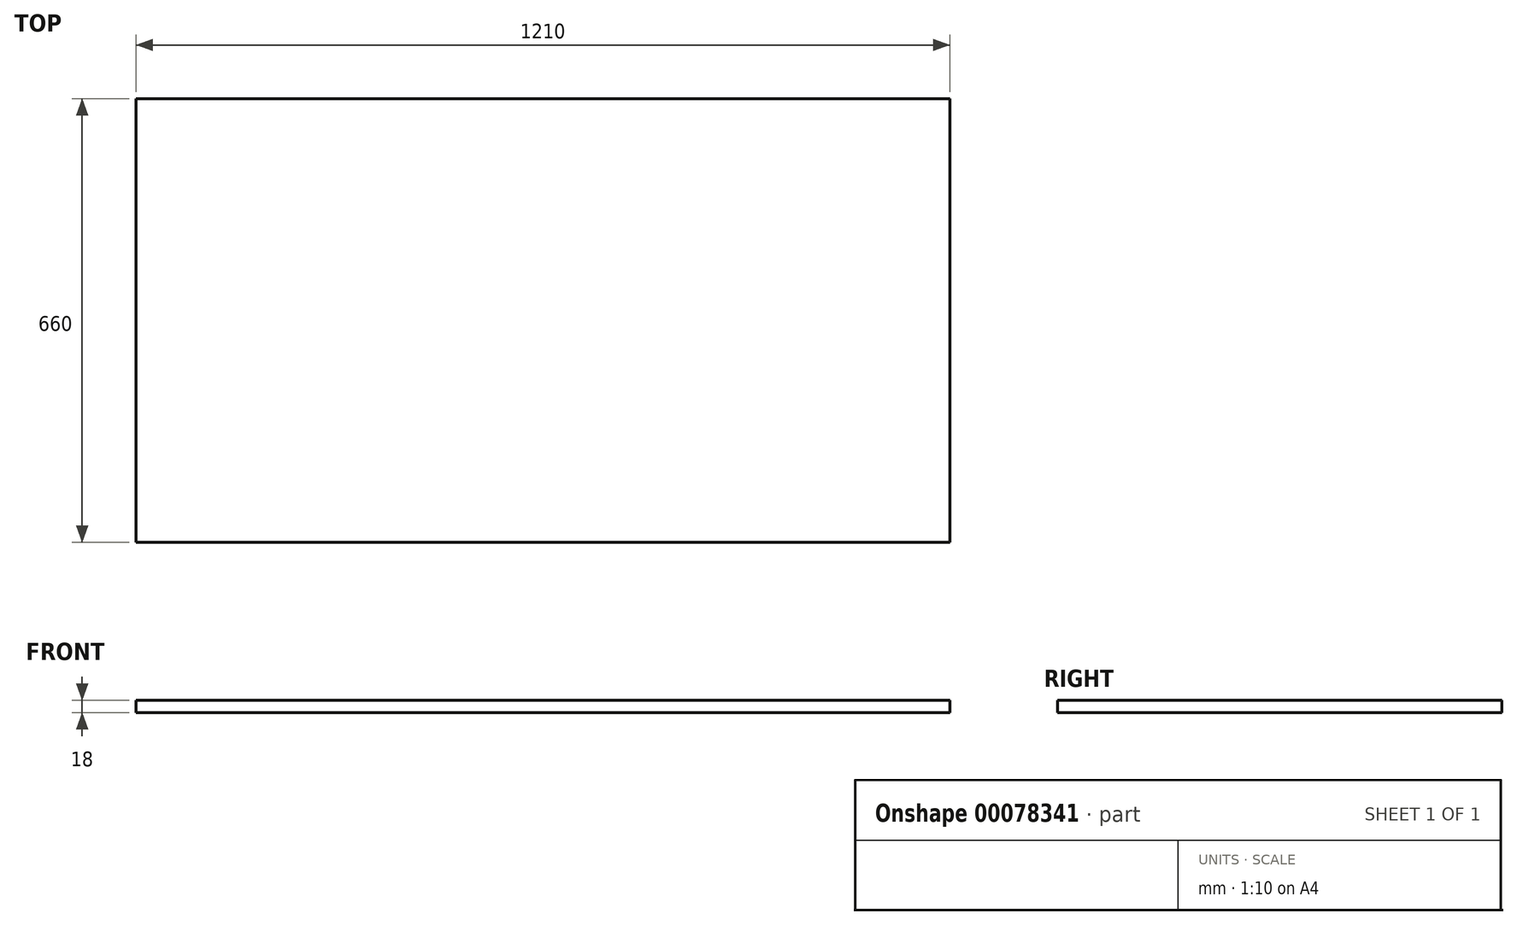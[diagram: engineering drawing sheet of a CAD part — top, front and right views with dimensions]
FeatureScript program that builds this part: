
annotation { "Feature Type Name" : "Feature", "Feature Type Description" : "" }
export const myFeature = defineFeature(function(context is Context, id is Id, definition is map)
    precondition{}
    {
        {
            var Q0;
            Q0=qCreatedBy(makeId("Top.planeOp"),FACE);
            var sketch = newSketch(context, id + "F0", { "sketchPlane" : qUnion([Q0])});
            skLineSegment(sketch, "E0", {"start": v(0, 0) * mm, "end": v(0, 935.46) * mm, "construction": true});
            skLineSegment(sketch, "E1.bottom", {"start": v(-605, 0) * mm, "end": v(605, 0) * mm});
            skLineSegment(sketch, "E1.top", {"start": v(-605, 660) * mm, "end": v(605, 660) * mm});
            skLineSegment(sketch, "E1.left", {"start": v(-605, 0) * mm, "end": v(-605, 660) * mm});
            skLineSegment(sketch, "E1.right", {"start": v(605, 0) * mm, "end": v(605, 660) * mm});
            skLineSegment(sketch, "E2.bottom", {"start": v(-402.5, 630) * mm, "end": v(-202.5, 630) * mm});
            skLineSegment(sketch, "E2.top", {"start": v(-402.5, 525) * mm, "end": v(-202.5, 525) * mm});
            skLineSegment(sketch, "E3.bottom", {"start": v(202.5, 630) * mm, "end": v(402.5, 630) * mm});
            skLineSegment(sketch, "E3.top", {"start": v(202.5, 525) * mm, "end": v(402.5, 525) * mm});
            skArc(sketch, "E4", {"start": v(-202.5, 630) * mm, "mid": v(-150, 577.5) * mm, "end": v(-202.5, 525) * mm});
            skArc(sketch, "E5", {"start": v(-402.5, 630) * mm, "mid": v(-455, 577.5) * mm, "end": v(-402.5, 525) * mm});
            skArc(sketch, "E6", {"start": v(202.5, 630) * mm, "mid": v(150, 577.5) * mm, "end": v(202.5, 525) * mm});
            skArc(sketch, "E7", {"start": v(402.5, 630) * mm, "mid": v(455, 577.5) * mm, "end": v(402.5, 525) * mm});
            skSolve(sketch);
        }
        {
            var Q0;
            Q0=makeQuery(id+"F0.imprint","IMPRINT",FACE,{"disambiguationData":[TD([[makeQuery(id+"F0.imprint","IMPRINT",EDGE,{"derivedFrom":sQuery(id+"F0.wireOp",EDGE,"E1.bottom")}),1.0]])]});
            var Q1;
            Q1=makeQuery(id+"F0.imprint","IMPRINT",FACE,{"disambiguationData":[TD([[makeQuery(id+"F0.imprint","IMPRINT",EDGE,{"derivedFrom":sQuery(id+"F0.wireOp",EDGE,"E2.bottom")}),-1.0]])]});
            var Q2;
            Q2=makeQuery(id+"F0.imprint","IMPRINT",FACE,{"disambiguationData":[TD([[makeQuery(id+"F0.imprint","IMPRINT",EDGE,{"derivedFrom":sQuery(id+"F0.wireOp",EDGE,"E3.bottom")}),-1.0]])]});
            extrude(context, id + "F1", {"entities" : qUnion([Q0, Q1, Q2]), "depth" : 18 * mm, "offsetDistance" : 25 * mm});
        }
    });
